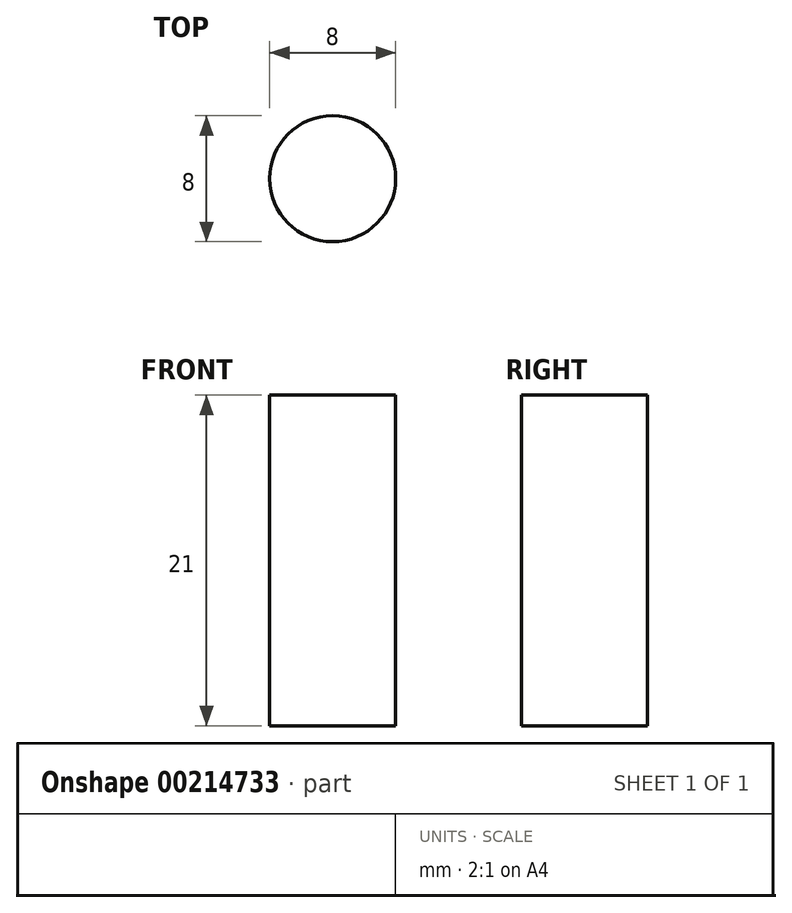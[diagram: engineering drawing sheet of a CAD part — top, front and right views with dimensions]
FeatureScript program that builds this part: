
annotation { "Feature Type Name" : "Feature", "Feature Type Description" : "" }
export const myFeature = defineFeature(function(context is Context, id is Id, definition is map)
    precondition{}
    {
        {
            assignVariable(context, id + "F0", {"name" : "ZZW", "anyValue" : 7});
        }
        {
            var Q0;
            Q0=qCreatedBy(makeId("Top.planeOp"),FACE);
            var sketch = newSketch(context, id + "F1", { "sketchPlane" : qUnion([Q0])});
            skCircle(sketch, "E0", {"center": v(0, 0) * mm, "radius": 4 * mm});
            skSolve(sketch);
        }
        {
            var Q0;
            Q0=makeQuery(id+"F1.imprint","IMPRINT",FACE,{"disambiguationData":[TD([[makeQuery(id+"F1.imprint","IMPRINT",EDGE,{"derivedFrom":sQuery(id+"F1.wireOp",EDGE,"E0")}),1.0]])]});
            extrude(context, id + "F2", {"entities" : qUnion([Q0]), "depth" : (getVariable(context, 'ZZW') * 3) * mm});
        }
    });
